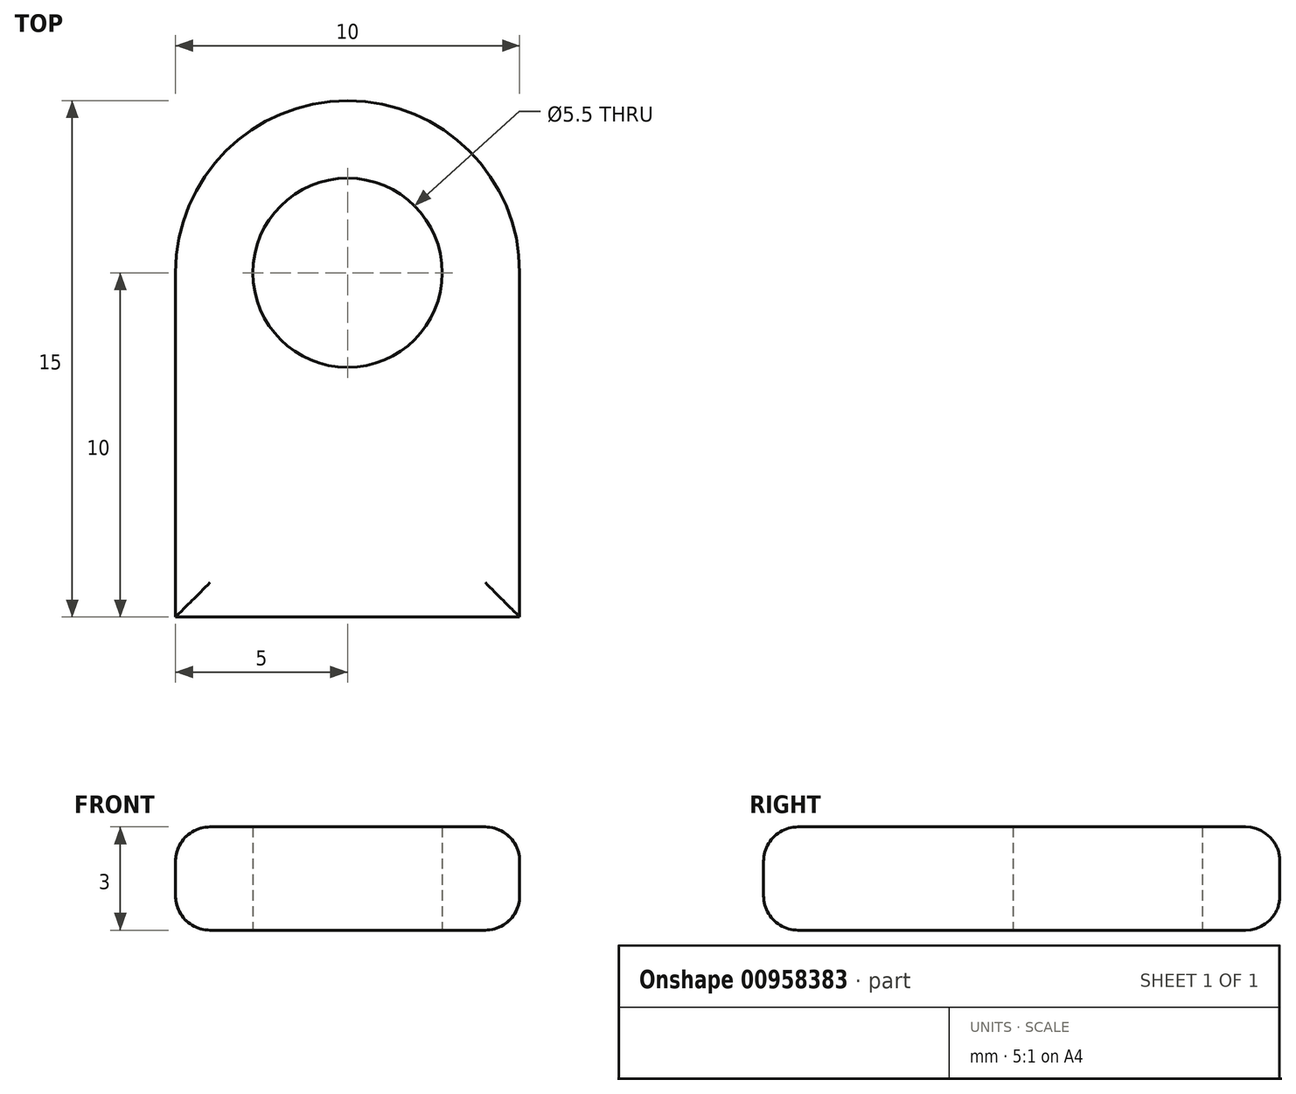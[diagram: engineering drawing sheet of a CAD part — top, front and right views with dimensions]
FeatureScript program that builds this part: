
annotation { "Feature Type Name" : "Feature", "Feature Type Description" : "" }
export const myFeature = defineFeature(function(context is Context, id is Id, definition is map)
    precondition{}
    {
        {
            var Q0;
            Q0=qCreatedBy(makeId("Top.planeOp"),FACE);
            var sketch = newSketch(context, id + "F0", { "sketchPlane" : qUnion([Q0])});
            skCircle(sketch, "E0", {"center": v(0, 0) * mm, "radius": 5 * mm});
            skCircle(sketch, "E1", {"center": v(0, 0) * mm, "radius": 2.75 * mm});
            skLineSegment(sketch, "E2", {"start": v(-5, 0) * mm, "end": v(-5, -10) * mm});
            skLineSegment(sketch, "E3", {"start": v(5, 0) * mm, "end": v(5, -10) * mm});
            skLineSegment(sketch, "E4", {"start": v(-5, -10) * mm, "end": v(5, -10) * mm});
            skSolve(sketch);
        }
        {
            var Q0;
            {var subQ0=sQuery(id+"F0.wireOp",EDGE,"E2");Q0=makeQuery(id+"F0.imprint","IMPRINT",FACE,{"disambiguationData":[TD([[makeQuery(id+"F0.imprint","IMPRINT",EDGE,{"derivedFrom":subQ0}),1.0]])]});}
            var Q1;
            Q1=makeQuery(id+"F0.imprint","IMPRINT",FACE,{"disambiguationData":[TD([[makeQuery(id+"F0.imprint","IMPRINT",EDGE,{"derivedFrom":sQuery(id+"F0.wireOp",EDGE,"E1")}),-1.0]])]});
            extrude(context, id + "F1", {"entities" : qUnion([Q0, Q1]), "depth" : 3 * mm, "offsetDistance" : 25 * mm});
        }
        {
            var Q0;
            Q0=makeQuery(id+"F1.opExtrude","CAP_EDGE",EDGE,{"disambiguationData":[OSD([sQuery(id+"F0.wireOp",EDGE,"E3")])],"isStart":true});
            var Q1;
            Q1=makeQuery(id+"F1.opExtrude","CAP_EDGE",EDGE,{"disambiguationData":[OSD([sQuery(id+"F0.wireOp",EDGE,"E3")])],"isStart":false});
            var Q2;
            Q2=makeQuery(id+"F1.opExtrude","CAP_EDGE",EDGE,{"disambiguationData":[OSD([sQuery(id+"F0.wireOp",EDGE,"E4")])],"isStart":false});
            var Q3;
            Q3=makeQuery(id+"F1.opExtrude","CAP_EDGE",EDGE,{"disambiguationData":[OSD([sQuery(id+"F0.wireOp",EDGE,"E0")])],"isStart":true});
            var Q4;
            Q4=makeQuery(id+"F1.opExtrude","CAP_EDGE",EDGE,{"disambiguationData":[OSD([sQuery(id+"F0.wireOp",EDGE,"E0")])],"isStart":false});
            var Q5;
            Q5=makeQuery(id+"F1.opExtrude","CAP_EDGE",EDGE,{"disambiguationData":[OSD([sQuery(id+"F0.wireOp",EDGE,"E2")])],"isStart":true});
            var Q6;
            Q6=makeQuery(id+"F1.opExtrude","CAP_EDGE",EDGE,{"disambiguationData":[OSD([sQuery(id+"F0.wireOp",EDGE,"E2")])],"isStart":false});
            var Q7;
            Q7=makeQuery(id+"F1.opExtrude","CAP_EDGE",EDGE,{"disambiguationData":[OSD([sQuery(id+"F0.wireOp",EDGE,"E4")])],"isStart":true});
            fillet(context, id + "F2", {"entities" : qUnion([Q0, Q1, Q2, Q3, Q4, Q5, Q6, Q7]), "radius" : 1 * mm, "allowEdgeOverflow" : false});
        }
    });
